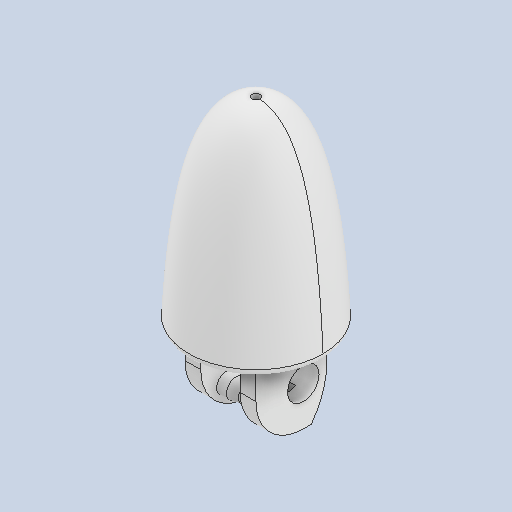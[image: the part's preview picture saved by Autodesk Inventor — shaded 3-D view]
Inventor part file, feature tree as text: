
AUTODESK INVENTOR PART (.ipt)
format: ipt  version: 2022 (Build 260153000, 153)  size: 278,528 bytes
history: native  units: in
note: dims shown in document units (in); Inventor stores cm internally (conversion verified against a paired STEP export)
features: sketch x6, fillet x5, extrude x4, hole x2, chamfer x2, plane x1, revolve x1
ambient origin geometry x8: Origin, YZ Plane, XZ Plane, XY Plane, X Axis, Y Axis, Z Axis, Center Point
bodies: Solid1 (feature_tree)
feature tree (21):
  extrude  "Extrusion1"  Depth=0.3937in
  extrude  "Extrusion2"  Depth=0.0394in TaperAngle=0.0deg
  fillet  "Fillet3"  Radius=0.0394in
  fillet  "Fillet4"  Radius=0.0394in
  fillet  "Fillet5"  Radius=0.2362in
  fillet  "Fillet6"  Radius=0.3937in
  hole  "Hole1"  [1 undecoded]
  extrude  "Extrusion3"  Depth=0.0984in TaperAngle=0.0deg
  chamfer  "Chamfer1"  Distance=0.0098in Angle=45.0deg
  extrude  "Extrusion4"  Depth=0.0394in
  chamfer  "Chamfer2"  Angle=90.0deg  [1 undecoded]
  plane  "Work Plane1"
  revolve  "Revolution1"  [1 undecoded]
  hole  "Hole2"  [1 undecoded]
  fillet  "Fillet7"  [1 undecoded]
  sketch  "Sketch1"  dims[d8=0.3937in d9=0.0in d11=0.6693in]
  sketch  "Sketch2"  dims[d12=0.0984in d13=0.0394in d14=0.0in d18=0.0394in d19=0.0394in d22=0.2362in d23=0.3937in]
  sketch  "Sketch3"  dims[d24=0.1969in]
  sketch  "Sketch4"  dims[d25=0.1575in d26=0.2362in d27=0.1575in d28=0.0787in d29=90.0deg d30=0.3937in d31=0.0in d36=0.0984in d37=0.0in]
  sketch  "Sketch7"  dims[d38=0.0098in d39=0.0492in d40=45.0deg d41=0.0984in d42=0.0in d43=0.0098in d44=0.0492in d45=45.0deg]
  sketch  "Sketch8"  dims[d48=0.9843in d49=0.9449in d50=90.0deg d51=0.0394in d52=0.2362in d53=0.1575in d54=0.0787in d55=90.0deg d56=1.5748in d57=0.0in d58=0.0394in]
note: 5 required parameter values undecoded (feature->parameter linkage not recoverable at this tier; creation-order binding heuristic only, values carry confidence <= 0.55)